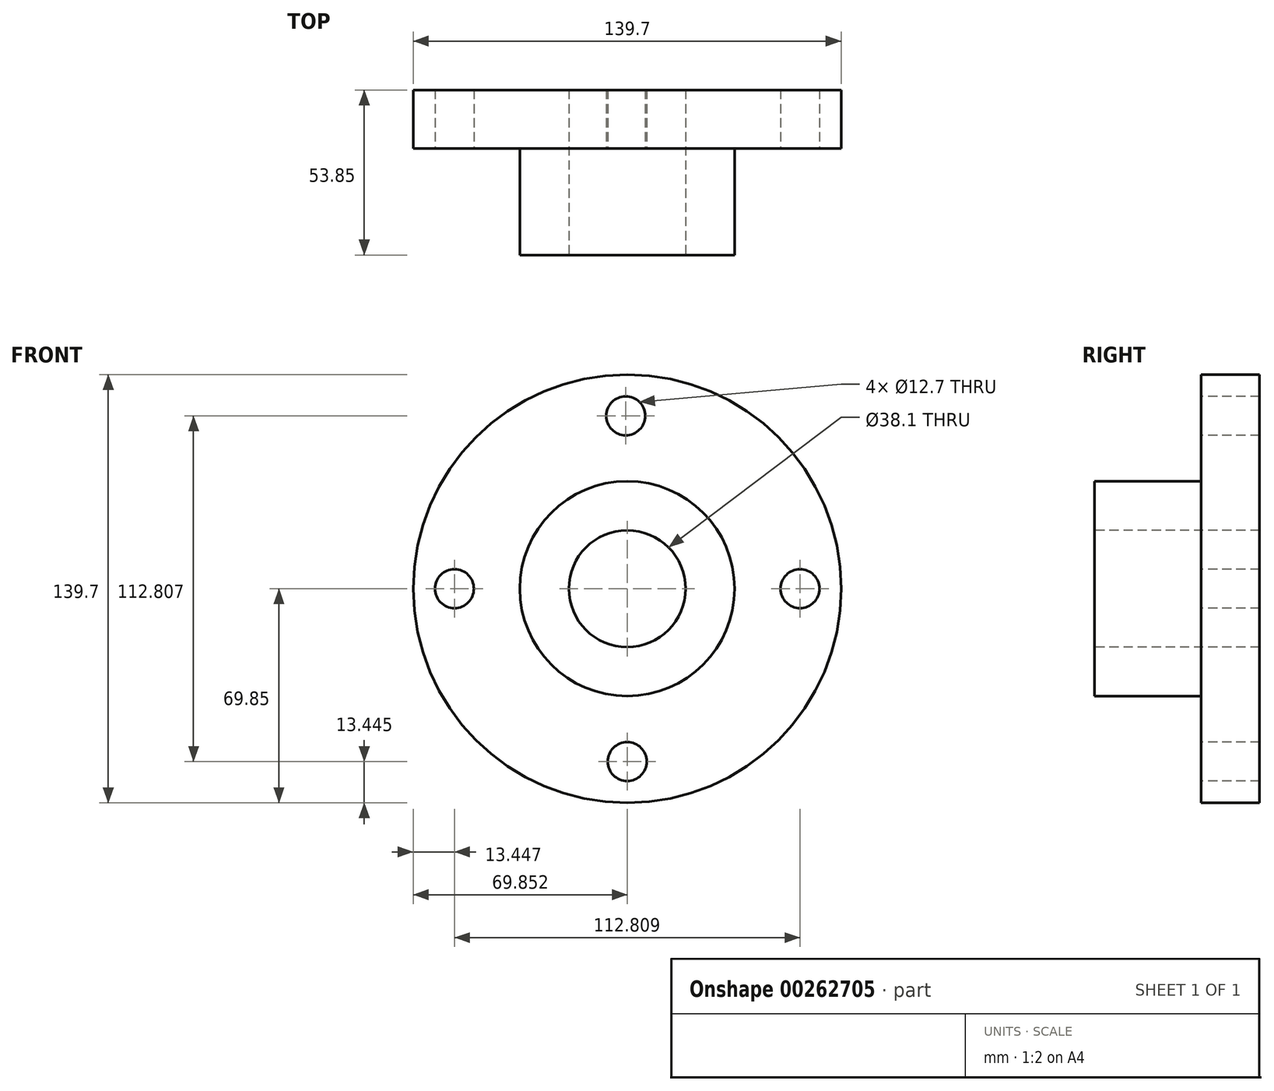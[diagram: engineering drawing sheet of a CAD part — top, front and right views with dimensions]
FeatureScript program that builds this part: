
annotation { "Feature Type Name" : "Feature", "Feature Type Description" : "" }
export const myFeature = defineFeature(function(context is Context, id is Id, definition is map)
    precondition{}
    {
        {
            var Q0;
            Q0=qCreatedBy(makeId("Top.planeOp"),FACE);
            var sketch = newSketch(context, id + "F0", { "sketchPlane" : qUnion([Q0])});
            skLineSegment(sketch, "E0", {"start": v(9.75, 15.14) * mm, "end": v(9.75, 69) * mm});
            skLineSegment(sketch, "E1", {"start": v(9.75, 69) * mm, "end": v(79.6, 69) * mm});
            skLineSegment(sketch, "E2", {"start": v(79.6, 69) * mm, "end": v(79.6, 49.94) * mm});
            skLineSegment(sketch, "E3", {"start": v(79.6, 49.94) * mm, "end": v(44.8, 49.94) * mm});
            skLineSegment(sketch, "E4", {"start": v(44.8, 49.94) * mm, "end": v(44.8, 15.14) * mm});
            skLineSegment(sketch, "E5", {"start": v(44.8, 15.14) * mm, "end": v(9.75, 15.14) * mm});
            skSolve(sketch);
        }
        {
            var Q0;
            Q0=makeQuery(id+"F0.imprint","IMPRINT",FACE,{"disambiguationData":[TD([[makeQuery(id+"F0.imprint","IMPRINT",EDGE,{"derivedFrom":sQuery(id+"F0.wireOp",EDGE,"E0")}),-1.0]])]});
            var Q1;
            Q1=sQuery(id+"F0.wireOp",EDGE,"E0");
            revolve(context, id + "F1", {"entities" : qUnion([Q0]), "axis" : qUnion([Q1]), "revolveType" : RevolveType.FULL});
        }
        {
            var Q0;
            Q0=makeQuery(id+"F1.opRevolve","SWEPT_FACE",FACE,{"disambiguationData":[OSD([sQuery(id+"F0.wireOp",EDGE,"E5")])]});
            var sketch = newSketch(context, id + "F2", { "sketchPlane" : qUnion([Q0])});
            skCircle(sketch, "E6", {"center": v(9.75, 0) * mm, "radius": 19.05 * mm});
            skSolve(sketch);
        }
        {
            var Q0;
            Q0 = qSketchRegion(id + "F2", true);
            extrude(context, id + "F3", {"entities" : qUnion([Q0]), "operationType" : NewBodyOperationType.REMOVE, "oppositeDirection" : true, "depth" : 108.97 * mm});
        }
        {
            var Q0;
            Q0=makeQuery(id+"F1.opRevolve","SWEPT_FACE",FACE,{"disambiguationData":[OSD([sQuery(id+"F0.wireOp",EDGE,"E3")])]});
            var sketch = newSketch(context, id + "F4", { "sketchPlane" : qUnion([Q0])});
            skCircle(sketch, "E7", {"center": v(9.27, 56.4) * mm, "radius": 6.35 * mm});
            skCircle(sketch, "E8", {"center": v(66.16, 0) * mm, "radius": 6.35 * mm});
            skCircle(sketch, "E9", {"center": v(-46.65, 0) * mm, "radius": 6.35 * mm});
            skCircle(sketch, "E10", {"center": v(9.75, -56.4) * mm, "radius": 6.35 * mm});
            skSolve(sketch);
        }
        {
            var Q0;
            Q0 = qSketchRegion(id + "F4", true);
            extrude(context, id + "F5", {"entities" : qUnion([Q0]), "operationType" : NewBodyOperationType.REMOVE, "oppositeDirection" : true, "depth" : 115.32 * mm});
        }
    });
